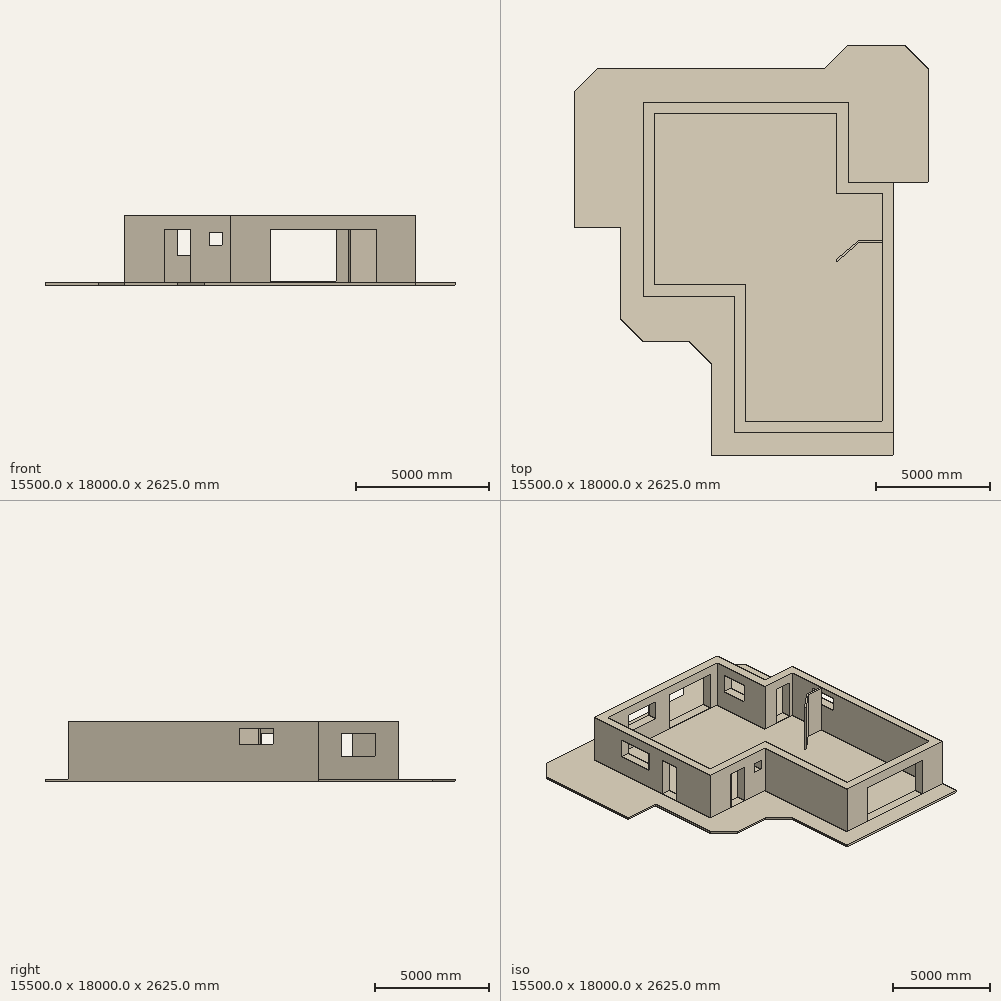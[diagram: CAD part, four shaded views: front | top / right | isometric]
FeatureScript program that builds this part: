
annotation { "Feature Type Name" : "Feature", "Feature Type Description" : "" }
export const myFeature = defineFeature(function(context is Context, id is Id, definition is map)
    precondition{}
    {
        {
            var Q0;
            Q0=qCreatedBy(makeId("Top.planeOp"),FACE);
            var sketch = newSketch(context, id + "F0", { "sketchPlane" : qUnion([Q0])});
            skLineSegment(sketch, "E0.bottom", {"start": v(0, 0) * mm, "end": v(8000, 0) * mm});
            skLineSegment(sketch, "E0.top", {"start": v(0, -7500) * mm, "end": v(4000, -7500) * mm});
            skLineSegment(sketch, "E0.left", {"start": v(0, 0) * mm, "end": v(0, -7500) * mm});
            skLineSegment(sketch, "E0.right", {"start": v(8000, 0) * mm, "end": v(8000, -3500) * mm});
            skLineSegment(sketch, "E1.top", {"start": v(10003.12, -13500) * mm, "end": v(4000, -13500) * mm});
            skLineSegment(sketch, "E1.right", {"start": v(4000, -7500) * mm, "end": v(4000, -13500) * mm});
            skLineSegment(sketch, "E2.bottom", {"start": v(8000, -3500) * mm, "end": v(10000, -3500) * mm});
            skLineSegment(sketch, "E2.top", {"start": v(4000, -13500) * mm, "end": v(10000, -13500) * mm});
            skLineSegment(sketch, "E2.right", {"start": v(10000, -3500) * mm, "end": v(10000, -13500) * mm});
            skLineSegment(sketch, "E3.0", {"start": v(3500, -8000) * mm, "end": v(3500, -14000) * mm});
            skLineSegment(sketch, "E3.1", {"start": v(-500, -8000) * mm, "end": v(3500, -8000) * mm});
            skLineSegment(sketch, "E3.2", {"start": v(3500, -14000) * mm, "end": v(10500, -14000) * mm});
            skLineSegment(sketch, "E3.3", {"start": v(-500, 500) * mm, "end": v(-500, -8000) * mm});
            skLineSegment(sketch, "E3.4", {"start": v(10500, -3000) * mm, "end": v(10500, -14000) * mm});
            skLineSegment(sketch, "E3.5", {"start": v(8500, -3000) * mm, "end": v(10500, -3000) * mm});
            skLineSegment(sketch, "E3.6", {"start": v(8500, 500) * mm, "end": v(8500, -3000) * mm});
            skLineSegment(sketch, "E3.7", {"start": v(-500, 500) * mm, "end": v(8500, 500) * mm});
            skSolve(sketch);
        }
        {
            var Q0;
            Q0 = qSketchRegion(id + "F0", true);
            extrude(context, id + "F1", {"entities" : qUnion([Q0]), "depth" : 2500 * mm, "offsetDistance" : 25 * mm, "hasSecondDirection" : true, "secondDirectionOppositeDirection" : true, "secondDirectionDepth" : 25 * mm});
        }
        {
            var Q0;
            Q0=makeQuery(id+"F1.opExtrude","SWEPT_FACE",FACE,{"disambiguationData":[OSD([sQuery(id+"F0.wireOp",EDGE,"E3.1")])]});
            var sketch = newSketch(context, id + "F2", { "sketchPlane" : qUnion([Q0])});
            skLineSegment(sketch, "E4.bottom", {"start": v(1000, 1985) * mm, "end": v(2000, 1985) * mm});
            skLineSegment(sketch, "E4.top", {"start": v(1000, -15) * mm, "end": v(2000, -15) * mm});
            skLineSegment(sketch, "E4.left", {"start": v(1000, 1985) * mm, "end": v(1000, -15) * mm});
            skLineSegment(sketch, "E4.right", {"start": v(2000, 1985) * mm, "end": v(2000, -15) * mm});
            skLineSegment(sketch, "E5.bottom", {"start": v(2700, 1875) * mm, "end": v(3200, 1875) * mm});
            skLineSegment(sketch, "E5.top", {"start": v(2700, 1375) * mm, "end": v(3200, 1375) * mm});
            skLineSegment(sketch, "E5.left", {"start": v(2700, 1875) * mm, "end": v(2700, 1375) * mm});
            skLineSegment(sketch, "E5.right", {"start": v(3200, 1875) * mm, "end": v(3200, 1375) * mm});
            skSolve(sketch);
        }
        {
            var Q0;
            Q0 = qSketchRegion(id + "F2", true);
            extrude(context, id + "F3", {"entities" : qUnion([Q0]), "operationType" : NewBodyOperationType.REMOVE, "endBound" : BoundingType.UP_TO_NEXT, "oppositeDirection" : true, "depth" : 25 * mm, "offsetDistance" : 25 * mm});
        }
        {
            var Q0;
            Q0=makeQuery(id+"F1.opExtrude","CAP_FACE",FACE,{"disambiguationData":[OSD([sQuery(id+"F0.wireOp",EDGE,"E0.bottom"),sQuery(id+"F0.wireOp",EDGE,"E0.top"),sQuery(id+"F0.wireOp",EDGE,"E0.left"),sQuery(id+"F0.wireOp",EDGE,"E0.right"),sQuery(id+"F0.wireOp",EDGE,"E1.top"),sQuery(id+"F0.wireOp",EDGE,"E1.left"),sQuery(id+"F0.wireOp",EDGE,"E1.right"),sQuery(id+"F0.wireOp",EDGE,"334608d4-50cf-46a8-ad73-65acd27ec0f9.0"),sQuery(id+"F0.wireOp",EDGE,"334608d4-50cf-46a8-ad73-65acd27ec0f9.1"),sQuery(id+"F0.wireOp",EDGE,"334608d4-50cf-46a8-ad73-65acd27ec0f9.2"),sQuery(id+"F0.wireOp",EDGE,"334608d4-50cf-46a8-ad73-65acd27ec0f9.3"),sQuery(id+"F0.wireOp",EDGE,"334608d4-50cf-46a8-ad73-65acd27ec0f9.4"),sQuery(id+"F0.wireOp",EDGE,"334608d4-50cf-46a8-ad73-65acd27ec0f9.5"),sQuery(id+"F0.wireOp",EDGE,"334608d4-50cf-46a8-ad73-65acd27ec0f9.6")])],"isStart":true});
            var sketch = newSketch(context, id + "F4", { "sketchPlane" : qUnion([Q0])});
            skLineSegment(sketch, "E6", {"start": v(-2500, -2000) * mm, "end": v(7500, -2000) * mm});
            skLineSegment(sketch, "E7", {"start": v(7500, -2000) * mm, "end": v(8500, -3000) * mm});
            skLineSegment(sketch, "E8", {"start": v(8500, -3000) * mm, "end": v(11000, -3000) * mm});
            skLineSegment(sketch, "E9", {"start": v(11000, -3000) * mm, "end": v(12000, -2000) * mm});
            skLineSegment(sketch, "E10", {"start": v(12000, -2000) * mm, "end": v(12000, 3000) * mm});
            skLineSegment(sketch, "E11", {"start": v(12000, 3000) * mm, "end": v(10500, 3000) * mm});
            skLineSegment(sketch, "E12", {"start": v(-2500, -2000) * mm, "end": v(-3500, -1000) * mm});
            skLineSegment(sketch, "E13", {"start": v(-3500, -1000) * mm, "end": v(-3500, 5000) * mm});
            skLineSegment(sketch, "E14", {"start": v(-3500, 5000) * mm, "end": v(-1500, 5000) * mm});
            skLineSegment(sketch, "E15", {"start": v(-1500, 5000) * mm, "end": v(-1500, 9000) * mm});
            skLineSegment(sketch, "E16", {"start": v(-1500, 9000) * mm, "end": v(-500, 10000) * mm});
            skLineSegment(sketch, "E17", {"start": v(-500, 10000) * mm, "end": v(1500, 10000) * mm});
            skLineSegment(sketch, "E18", {"start": v(1500, 10000) * mm, "end": v(2500, 11000) * mm});
            skLineSegment(sketch, "E19", {"start": v(2500, 11000) * mm, "end": v(2500, 15000) * mm});
            skLineSegment(sketch, "E20", {"start": v(2500, 15000) * mm, "end": v(10500, 15000) * mm});
            skLineSegment(sketch, "E21", {"start": v(10500, 15000) * mm, "end": v(10500, 14000) * mm});
            skLineSegment(sketch, "E22", {"start": v(10500, 3000) * mm, "end": v(10500, 14000) * mm});
            skSolve(sketch);
        }
        {
            var Q0;
            Q0 = qSketchRegion(id + "F4", true);
            extrude(context, id + "F5", {"entities" : qUnion([Q0]), "operationType" : NewBodyOperationType.ADD, "depth" : 100 * mm, "offsetDistance" : 25 * mm});
        }
        {
            var Q0;
            Q0=makeQuery(id+"F1.opExtrude","SWEPT_FACE",FACE,{"disambiguationData":[OSD([sQuery(id+"F0.wireOp",EDGE,"E3.7")])]});
            var sketch = newSketch(context, id + "F6", { "sketchPlane" : qUnion([Q0])});
            skLineSegment(sketch, "E23.bottom", {"start": v(-7500, 2010) * mm, "end": v(-4500, 2010) * mm});
            skLineSegment(sketch, "E23.left", {"start": v(-7500, 2010) * mm, "end": v(-7500, 10) * mm});
            skLineSegment(sketch, "E23.right", {"start": v(-4500, 2010) * mm, "end": v(-4500, 10) * mm});
            skLineSegment(sketch, "E24.bottom", {"start": v(-3500, 2000) * mm, "end": v(-1500, 2000) * mm});
            skLineSegment(sketch, "E24.top", {"start": v(-3500, 1000) * mm, "end": v(-1500, 1000) * mm});
            skLineSegment(sketch, "E24.left", {"start": v(-3500, 2000) * mm, "end": v(-3500, 1000) * mm});
            skLineSegment(sketch, "E24.right", {"start": v(-1500, 2000) * mm, "end": v(-1500, 1000) * mm});
            skLineSegment(sketch, "E25", {"start": v(-7500, 10) * mm, "end": v(-4500, 10) * mm});
            skSolve(sketch);
        }
        {
            var Q0;
            Q0 = qSketchRegion(id + "F6", true);
            extrude(context, id + "F7", {"entities" : qUnion([Q0]), "operationType" : NewBodyOperationType.REMOVE, "endBound" : BoundingType.UP_TO_NEXT, "oppositeDirection" : true, "depth" : 25 * mm, "offsetDistance" : 25 * mm});
        }
        {
            var Q0;
            Q0=makeQuery(id+"F1.opExtrude","SWEPT_FACE",FACE,{"disambiguationData":[OSD([sQuery(id+"F0.wireOp",EDGE,"E3.5")])]});
            var sketch = newSketch(context, id + "F8", { "sketchPlane" : qUnion([Q0])});
            skLineSegment(sketch, "E26.bottom", {"start": v(-9800, 10) * mm, "end": v(-8800, 10) * mm});
            skLineSegment(sketch, "E26.top", {"start": v(-9800, 2010) * mm, "end": v(-8800, 2010) * mm});
            skLineSegment(sketch, "E26.left", {"start": v(-9800, 10) * mm, "end": v(-9800, 2010) * mm});
            skLineSegment(sketch, "E26.right", {"start": v(-8800, 10) * mm, "end": v(-8800, 2010) * mm});
            skSolve(sketch);
        }
        {
            var Q0;
            Q0 = qSketchRegion(id + "F8", true);
            extrude(context, id + "F9", {"entities" : qUnion([Q0]), "operationType" : NewBodyOperationType.REMOVE, "endBound" : BoundingType.UP_TO_NEXT, "oppositeDirection" : true, "depth" : 25 * mm, "offsetDistance" : 25 * mm});
        }
        {
            var Q0;
            Q0=makeQuery(id+"F1.opExtrude","SWEPT_FACE",FACE,{"disambiguationData":[OSD([sQuery(id+"F0.wireOp",EDGE,"E3.6")])]});
            var sketch = newSketch(context, id + "F10", { "sketchPlane" : qUnion([Q0])});
            skLineSegment(sketch, "E27.bottom", {"start": v(-2000, 1975) * mm, "end": v(-500, 1975) * mm});
            skLineSegment(sketch, "E27.top", {"start": v(-2000, 975) * mm, "end": v(-500, 975) * mm});
            skLineSegment(sketch, "E27.left", {"start": v(-2000, 1975) * mm, "end": v(-2000, 975) * mm});
            skLineSegment(sketch, "E27.right", {"start": v(-500, 1975) * mm, "end": v(-500, 975) * mm});
            skSolve(sketch);
        }
        {
            var Q0;
            Q0 = qSketchRegion(id + "F10", true);
            extrude(context, id + "F11", {"entities" : qUnion([Q0]), "operationType" : NewBodyOperationType.REMOVE, "endBound" : BoundingType.UP_TO_NEXT, "oppositeDirection" : true, "depth" : 25 * mm, "offsetDistance" : 25 * mm});
        }
        {
            var Q0;
            Q0=makeQuery(id+"F1.opExtrude","SWEPT_FACE",FACE,{"disambiguationData":[OSD([sQuery(id+"F0.wireOp",EDGE,"E3.4")])]});
            var sketch = newSketch(context, id + "F12", { "sketchPlane" : qUnion([Q0])});
            skLineSegment(sketch, "E28.bottom", {"start": v(-6500, 2200) * mm, "end": v(-5000, 2200) * mm});
            skLineSegment(sketch, "E28.top", {"start": v(-6500, 1500) * mm, "end": v(-5000, 1500) * mm});
            skLineSegment(sketch, "E28.left", {"start": v(-6500, 2200) * mm, "end": v(-6500, 1500) * mm});
            skLineSegment(sketch, "E28.right", {"start": v(-5000, 2200) * mm, "end": v(-5000, 1500) * mm});
            skSolve(sketch);
        }
        {
            var Q0;
            Q0 = qSketchRegion(id + "F12", true);
            extrude(context, id + "F13", {"entities" : qUnion([Q0]), "operationType" : NewBodyOperationType.REMOVE, "endBound" : BoundingType.UP_TO_NEXT, "oppositeDirection" : true, "depth" : 25 * mm, "offsetDistance" : 25 * mm});
        }
        {
            var Q0;
            Q0=makeQuery(id+"F1.opExtrude","SWEPT_FACE",FACE,{"disambiguationData":[OSD([sQuery(id+"F0.wireOp",EDGE,"E3.3")])]});
            var sketch = newSketch(context, id + "F14", { "sketchPlane" : qUnion([Q0])});
            skLineSegment(sketch, "E29.bottom", {"start": v(4500, 1985) * mm, "end": v(5500, 1985) * mm});
            skLineSegment(sketch, "E29.left", {"start": v(4500, 1985) * mm, "end": v(4500, -15) * mm});
            skLineSegment(sketch, "E29.right", {"start": v(5500, 1985) * mm, "end": v(5500, -15) * mm});
            skLineSegment(sketch, "E30.bottom", {"start": v(1500, 1975) * mm, "end": v(3500, 1975) * mm});
            skLineSegment(sketch, "E30.top", {"start": v(1500, 975) * mm, "end": v(3500, 975) * mm});
            skLineSegment(sketch, "E30.left", {"start": v(1500, 1975) * mm, "end": v(1500, 975) * mm});
            skLineSegment(sketch, "E30.right", {"start": v(3500, 1975) * mm, "end": v(3500, 975) * mm});
            skLineSegment(sketch, "E31", {"start": v(4500, -15) * mm, "end": v(5500, -15) * mm});
            skSolve(sketch);
        }
        {
            var Q0;
            Q0 = qSketchRegion(id + "F14", true);
            extrude(context, id + "F15", {"entities" : qUnion([Q0]), "operationType" : NewBodyOperationType.REMOVE, "endBound" : BoundingType.UP_TO_NEXT, "oppositeDirection" : true, "depth" : 25 * mm, "offsetDistance" : 25 * mm});
        }
        {
            var Q0;
            Q0=makeQuery(id+"F1.opExtrude","SWEPT_FACE",FACE,{"disambiguationData":[OSD([sQuery(id+"F0.wireOp",EDGE,"E3.2")])]});
            var sketch = newSketch(context, id + "F16", { "sketchPlane" : qUnion([Q0])});
            skLineSegment(sketch, "E32.bottom", {"start": v(5000, 1985) * mm, "end": v(9000, 1985) * mm});
            skLineSegment(sketch, "E32.left", {"start": v(5000, 1985) * mm, "end": v(5000, -15) * mm});
            skLineSegment(sketch, "E32.right", {"start": v(9000, 1985) * mm, "end": v(9000, -15) * mm});
            skLineSegment(sketch, "E33", {"start": v(5000, -15) * mm, "end": v(9000, -15) * mm});
            skSolve(sketch);
        }
        {
            var Q0;
            Q0 = qSketchRegion(id + "F16", true);
            extrude(context, id + "F17", {"entities" : qUnion([Q0]), "operationType" : NewBodyOperationType.REMOVE, "endBound" : BoundingType.UP_TO_NEXT, "oppositeDirection" : true, "depth" : 25 * mm, "offsetDistance" : 25 * mm});
        }
        {
            var Q0;
            Q0=makeQuery(id+"F5.boolean.opBoolean","SPLIT",FACE,{"disambiguationData":[TD([makeQuery(id+"F1.opExtrude","SWEPT_FACE",FACE,{"disambiguationData":[OSD([sQuery(id+"F0.wireOp",EDGE,"E0.bottom")])]})])],"derivedFrom":makeQuery(id+"F5.opExtrude","CAP_FACE",FACE,{"disambiguationData":[OSD([sQuery(id+"F4.wireOp",EDGE,"E6"),sQuery(id+"F4.wireOp",EDGE,"E7"),sQuery(id+"F4.wireOp",EDGE,"E8"),sQuery(id+"F4.wireOp",EDGE,"E9"),sQuery(id+"F4.wireOp",EDGE,"E10"),sQuery(id+"F4.wireOp",EDGE,"E11"),sQuery(id+"F4.wireOp",EDGE,"E12"),sQuery(id+"F4.wireOp",EDGE,"E13"),sQuery(id+"F4.wireOp",EDGE,"E14"),sQuery(id+"F4.wireOp",EDGE,"E15"),sQuery(id+"F4.wireOp",EDGE,"E16"),sQuery(id+"F4.wireOp",EDGE,"E17"),sQuery(id+"F4.wireOp",EDGE,"E18"),sQuery(id+"F4.wireOp",EDGE,"E19"),sQuery(id+"F4.wireOp",EDGE,"E20"),sQuery(id+"F4.wireOp",EDGE,"E21"),sQuery(id+"F4.wireOp",EDGE,"E22")])],"isStart":true})});
            var sketch = newSketch(context, id + "F18", { "sketchPlane" : qUnion([Q0])});
            skLineSegment(sketch, "E34.bottom", {"start": v(10000, -5543.94) * mm, "end": v(9000, -5543.94) * mm});
            skLineSegment(sketch, "E34.top", {"start": v(10000, -5643.94) * mm, "end": v(9000, -5643.94) * mm});
            skLineSegment(sketch, "E34.left", {"start": v(10000, -5543.94) * mm, "end": v(10000, -5643.94) * mm});
            skLineSegment(sketch, "E35", {"start": v(9000, -5543.94) * mm, "end": v(7954.2, -6424.79) * mm});
            skLineSegment(sketch, "E36", {"start": v(7954.2, -6424.79) * mm, "end": v(8018.63, -6501.29) * mm});
            skLineSegment(sketch, "E37", {"start": v(8018.63, -6501.29) * mm, "end": v(9000, -5643.94) * mm});
            skSolve(sketch);
        }
        {
            var Q0;
            Q0 = qSketchRegion(id + "F18", true);
            extrude(context, id + "F19", {"entities" : qUnion([Q0]), "operationType" : NewBodyOperationType.ADD, "depth" : 2500 * mm, "offsetDistance" : 25 * mm});
        }
    });
